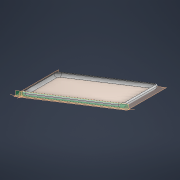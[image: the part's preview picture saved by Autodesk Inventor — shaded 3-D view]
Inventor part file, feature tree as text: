
AUTODESK INVENTOR PART (.ipt)
format: ipt  version: 2021 (Build 250183000, 183)  size: 176,128 bytes
history: native  units: mm
features: fillet x3, extrude x1, thicken_offset x1, sketch x1
ambient origin geometry x8: Origin, YZ Plane, XZ Plane, XY Plane, X Axis, Y Axis, Z Axis, Center Point
bodies: Solid1 (feature_tree), Solid2 (feature_tree)
feature tree (6):
  extrude  "Extrusion1"  Depth=0.8mm
  fillet  "Fillet1"  [1 undecoded]
  fillet  "Fillet2"  Radius=9.9mm
  fillet  "Fillet3"  Radius=5.9mm
  thicken_offset  "Thicken1"
  sketch  "Sketch1"  dims[d0=208.4mm d1=137.5mm d3=0.0mm d4=9.9mm d6=5.9mm d7=0.8mm d8=0.8mm]
note: 1 required parameter value undecoded (feature->parameter linkage not recoverable at this tier; creation-order binding heuristic only, values carry confidence <= 0.55)
